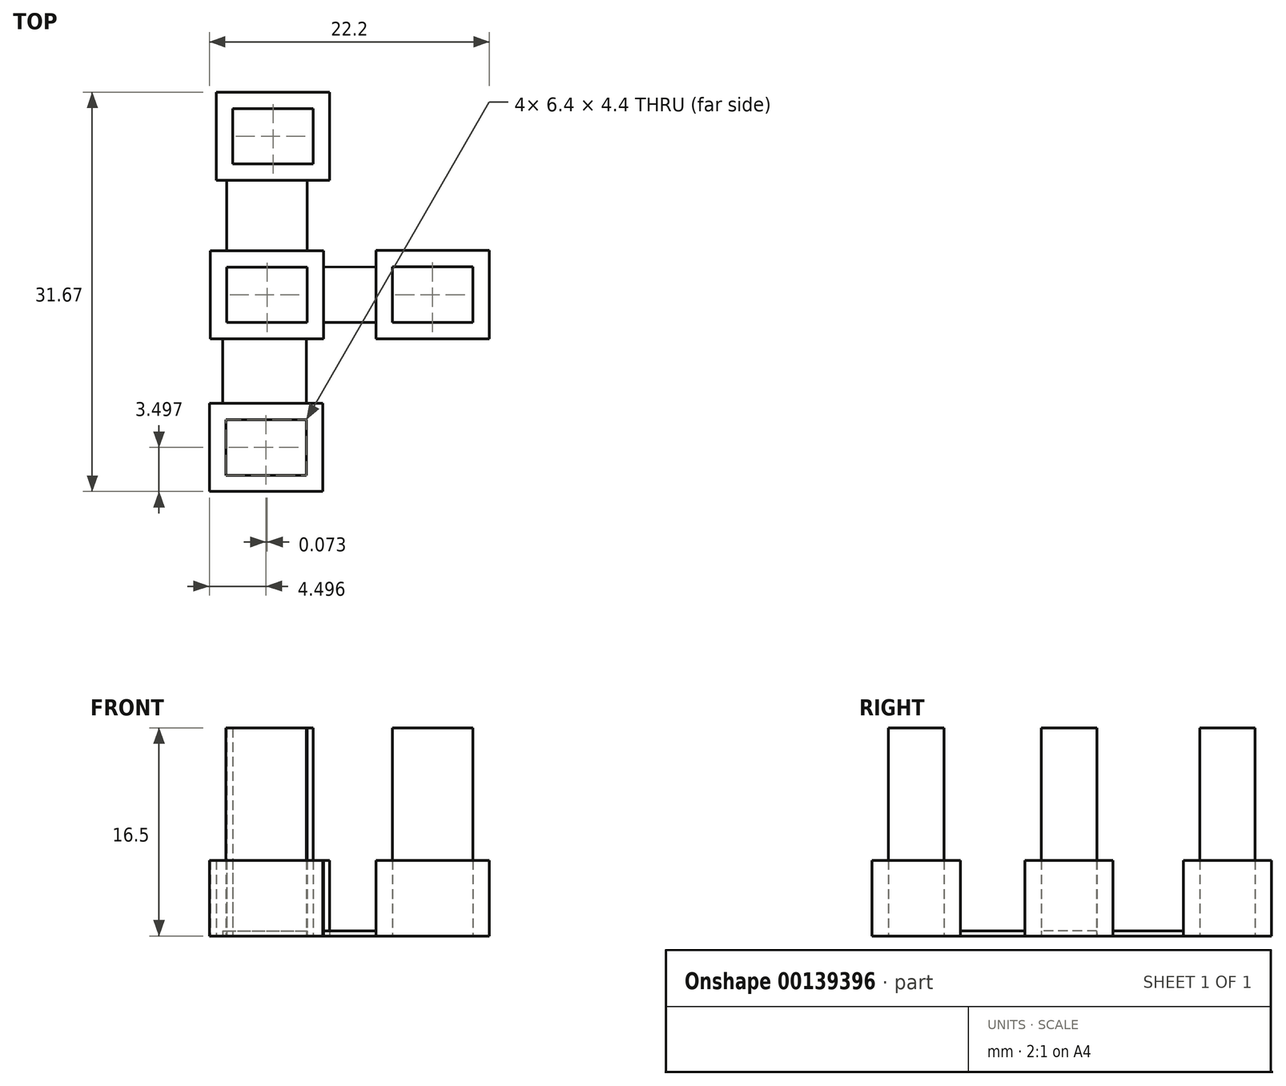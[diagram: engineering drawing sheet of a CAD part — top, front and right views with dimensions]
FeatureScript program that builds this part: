
annotation { "Feature Type Name" : "Feature", "Feature Type Description" : "" }
export const myFeature = defineFeature(function(context is Context, id is Id, definition is map)
    precondition{}
    {
        {
            var Q0;
            Q0=qCreatedBy(makeId("Top.planeOp"),FACE);
            var sketch = newSketch(context, id + "F0", { "sketchPlane" : qUnion([Q0])});
            skLineSegment(sketch, "E0", {"start": v(-34.37, 13) * mm, "end": v(-27.37, 8) * mm, "construction": true});
            skLineSegment(sketch, "E1", {"start": v(-27.37, 13) * mm, "end": v(-34.37, 8) * mm, "construction": true});
            skLineSegment(sketch, "E2", {"start": v(-34.84, 0.43) * mm, "end": v(-27.84, -4.57) * mm, "construction": true});
            skLineSegment(sketch, "E3", {"start": v(-27.84, 0.43) * mm, "end": v(-34.84, -4.57) * mm, "construction": true});
            skLineSegment(sketch, "E4", {"start": v(-34.91, -11.67) * mm, "end": v(-27.91, -16.67) * mm, "construction": true});
            skLineSegment(sketch, "E5", {"start": v(-27.91, -11.67) * mm, "end": v(-34.91, -16.67) * mm, "construction": true});
            skLineSegment(sketch, "E6", {"start": v(-21.7, 0.44) * mm, "end": v(-14.7, -4.56) * mm, "construction": true});
            skLineSegment(sketch, "E7", {"start": v(-14.7, 0.44) * mm, "end": v(-21.7, -4.56) * mm, "construction": true});
            skLineSegment(sketch, "E8.bottom", {"start": v(-35.37, 14) * mm, "end": v(-26.37, 14) * mm});
            skLineSegment(sketch, "E8.top", {"start": v(-35.37, 7) * mm, "end": v(-26.37, 7) * mm});
            skLineSegment(sketch, "E8.left", {"start": v(-35.37, 14) * mm, "end": v(-35.37, 7) * mm});
            skLineSegment(sketch, "E8.right", {"start": v(-26.37, 14) * mm, "end": v(-26.37, 7) * mm});
            skPoint(sketch, "E8.middle", {"position": v(-30.87, 10.5) * mm});
            skLineSegment(sketch, "E9.bottom", {"start": v(-35.84, 1.43) * mm, "end": v(-26.84, 1.43) * mm});
            skLineSegment(sketch, "E9.top", {"start": v(-35.84, -5.57) * mm, "end": v(-26.84, -5.57) * mm});
            skLineSegment(sketch, "E9.left", {"start": v(-35.84, 1.43) * mm, "end": v(-35.84, -5.57) * mm});
            skLineSegment(sketch, "E9.right", {"start": v(-26.84, 1.43) * mm, "end": v(-26.84, -5.57) * mm});
            skPoint(sketch, "E9.middle", {"position": v(-31.34, -2.07) * mm});
            skLineSegment(sketch, "E10.bottom", {"start": v(-35.91, -10.67) * mm, "end": v(-26.91, -10.67) * mm});
            skLineSegment(sketch, "E10.top", {"start": v(-35.91, -17.67) * mm, "end": v(-26.91, -17.67) * mm});
            skLineSegment(sketch, "E10.left", {"start": v(-35.91, -10.67) * mm, "end": v(-35.91, -17.67) * mm});
            skLineSegment(sketch, "E10.right", {"start": v(-26.91, -10.67) * mm, "end": v(-26.91, -17.67) * mm});
            skPoint(sketch, "E10.middle", {"position": v(-31.41, -14.17) * mm});
            skLineSegment(sketch, "E11.bottom", {"start": v(-22.7, 1.44) * mm, "end": v(-13.7, 1.44) * mm});
            skLineSegment(sketch, "E11.top", {"start": v(-22.7, -5.56) * mm, "end": v(-13.7, -5.56) * mm});
            skLineSegment(sketch, "E11.left", {"start": v(-22.7, 1.44) * mm, "end": v(-22.7, -5.56) * mm});
            skLineSegment(sketch, "E11.right", {"start": v(-13.7, 1.44) * mm, "end": v(-13.7, -5.56) * mm});
            skPoint(sketch, "E11.middle", {"position": v(-18.2, -2.06) * mm});
            skLineSegment(sketch, "E12.bottom", {"start": v(-34.07, 12.7) * mm, "end": v(-27.67, 12.7) * mm});
            skLineSegment(sketch, "E12.top", {"start": v(-34.07, 8.3) * mm, "end": v(-27.67, 8.3) * mm});
            skLineSegment(sketch, "E12.left", {"start": v(-34.07, 12.7) * mm, "end": v(-34.07, 8.3) * mm});
            skLineSegment(sketch, "E12.right", {"start": v(-27.67, 12.7) * mm, "end": v(-27.67, 8.3) * mm});
            skLineSegment(sketch, "E13.bottom", {"start": v(-34.54, 0.13) * mm, "end": v(-28.14, 0.13) * mm});
            skLineSegment(sketch, "E13.top", {"start": v(-34.54, -4.27) * mm, "end": v(-28.14, -4.27) * mm});
            skLineSegment(sketch, "E13.left", {"start": v(-34.54, 0.13) * mm, "end": v(-34.54, -4.27) * mm});
            skLineSegment(sketch, "E13.right", {"start": v(-28.14, 0.13) * mm, "end": v(-28.14, -4.27) * mm});
            skLineSegment(sketch, "E14.bottom", {"start": v(-34.61, -11.97) * mm, "end": v(-28.21, -11.97) * mm});
            skLineSegment(sketch, "E14.top", {"start": v(-34.61, -16.37) * mm, "end": v(-28.21, -16.37) * mm});
            skLineSegment(sketch, "E14.left", {"start": v(-34.61, -11.97) * mm, "end": v(-34.61, -16.37) * mm});
            skLineSegment(sketch, "E14.right", {"start": v(-28.21, -11.97) * mm, "end": v(-28.21, -16.37) * mm});
            skLineSegment(sketch, "E15.bottom", {"start": v(-21.4, 0.14) * mm, "end": v(-15, 0.14) * mm});
            skLineSegment(sketch, "E15.top", {"start": v(-21.4, -4.26) * mm, "end": v(-15, -4.26) * mm});
            skLineSegment(sketch, "E15.left", {"start": v(-21.4, 0.14) * mm, "end": v(-21.4, -4.26) * mm});
            skLineSegment(sketch, "E15.right", {"start": v(-15, 0.14) * mm, "end": v(-15, -4.26) * mm});
            skLineSegment(sketch, "E16", {"start": v(-34.84, -5.57) * mm, "end": v(-34.84, -10.67) * mm});
            skLineSegment(sketch, "E17", {"start": v(-28.21, -11.97) * mm, "end": v(-28.25, -11.92) * mm});
            skLineSegment(sketch, "E18", {"start": v(-28.21, -11.97) * mm, "end": v(-28.21, -11.89) * mm});
            skLineSegment(sketch, "E19", {"start": v(-34.54, 0.13) * mm, "end": v(-34.54, 0.22) * mm});
            skLineSegment(sketch, "E20", {"start": v(-28.14, 0.13) * mm, "end": v(-28.14, 0.22) * mm});
            skLineSegment(sketch, "E21", {"start": v(-26.84, 0.13) * mm, "end": v(-22.7, 0.14) * mm});
            skLineSegment(sketch, "E22", {"start": v(-26.84, -4.27) * mm, "end": v(-22.7, -4.26) * mm});
            skLineSegment(sketch, "E23.trimOffspring", {"start": v(-34.54, 1.43) * mm, "end": v(-34.54, 7) * mm});
            skLineSegment(sketch, "E24.trimOffspring", {"start": v(-28.14, 1.43) * mm, "end": v(-28.14, 7) * mm});
            skLineSegment(sketch, "E25.trimOffspring", {"start": v(-28.21, -10.67) * mm, "end": v(-28.21, -5.57) * mm});
            skSolve(sketch);
        }
        {
            var Q0;
            {var subQ7=sQuery(id+"F0.wireOp",EDGE,"E9.left");Q0=makeQuery(id+"F0.imprint","IMPRINT",FACE,{"disambiguationData":[TD([[makeQuery(id+"F0.imprint","IMPRINT",EDGE,{"derivedFrom":subQ7}),1.0]])]});}
            var Q1;
            {var subQ3=sQuery(id+"F0.wireOp",EDGE,"E11.bottom");Q1=makeQuery(id+"F0.imprint","IMPRINT",FACE,{"disambiguationData":[TD([[makeQuery(id+"F0.imprint","IMPRINT",EDGE,{"derivedFrom":subQ3}),-1.0]])]});}
            var Q2;
            Q2=makeQuery(id+"F0.imprint","IMPRINT",FACE,{"disambiguationData":[TD([[makeQuery(id+"F0.imprint","IMPRINT",EDGE,{"derivedFrom":sQuery(id+"F0.wireOp",EDGE,"E8.bottom")}),-1.0]])]});
            var Q3;
            Q3=makeQuery(id+"F0.imprint","IMPRINT",FACE,{"disambiguationData":[TD([[makeQuery(id+"F0.imprint","IMPRINT",EDGE,{"derivedFrom":sQuery(id+"F0.wireOp",EDGE,"E10.top")}),1.0]])]});
            extrude(context, id + "F1", {"entities" : qUnion([Q0, Q1, Q2, Q3]), "depth" : 6 * mm});
        }
        {
            var Q0;
            Q0=makeQuery(id+"F0.imprint","IMPRINT",FACE,{"disambiguationData":[TD([[makeQuery(id+"F0.imprint","IMPRINT",EDGE,{"derivedFrom":sQuery(id+"F0.wireOp",EDGE,"E12.bottom")}),-1.0]])]});
            var Q1;
            Q1=makeQuery(id+"F0.imprint","IMPRINT",FACE,{"disambiguationData":[TD([[makeQuery(id+"F0.imprint","IMPRINT",EDGE,{"derivedFrom":sQuery(id+"F0.wireOp",EDGE,"E13.bottom")}),-1.0]])]});
            var Q2;
            Q2=makeQuery(id+"F0.imprint","IMPRINT",FACE,{"disambiguationData":[TD([[makeQuery(id+"F0.imprint","IMPRINT",EDGE,{"derivedFrom":sQuery(id+"F0.wireOp",EDGE,"E15.bottom")}),-1.0]])]});
            var Q3;
            Q3=makeQuery(id+"F0.imprint","IMPRINT",FACE,{"disambiguationData":[TD([[makeQuery(id+"F0.imprint","IMPRINT",EDGE,{"derivedFrom":sQuery(id+"F0.wireOp",EDGE,"E14.bottom")}),-1.0]])]});
            extrude(context, id + "F2", {"entities" : qUnion([Q0, Q1, Q2, Q3]), "depth" : 16.5 * mm});
        }
        {
            var Q0;
            {var subQ0=sQuery(id+"F0.wireOp",EDGE,"E21");Q0=makeQuery(id+"F0.imprint","IMPRINT",FACE,{"disambiguationData":[TD([[makeQuery(id+"F0.imprint","IMPRINT",EDGE,{"derivedFrom":subQ0}),-1.0]])]});}
            var Q1;
            {var subQ0=sQuery(id+"F0.wireOp",EDGE,"E23.trimOffspring");Q1=makeQuery(id+"F0.imprint","IMPRINT",FACE,{"disambiguationData":[TD([[makeQuery(id+"F0.imprint","IMPRINT",EDGE,{"derivedFrom":subQ0}),-1.0]])]});}
            var Q2;
            {var subQ0=sQuery(id+"F0.wireOp",EDGE,"E16");Q2=makeQuery(id+"F0.imprint","IMPRINT",FACE,{"disambiguationData":[TD([[makeQuery(id+"F0.imprint","IMPRINT",EDGE,{"derivedFrom":subQ0}),1.0]])]});}
            extrude(context, id + "F3", {"entities" : qUnion([Q0, Q1, Q2]), "depth" : 0.4 * mm});
        }
    });
